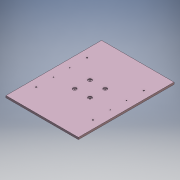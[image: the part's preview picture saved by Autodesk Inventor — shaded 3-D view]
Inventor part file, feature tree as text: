
AUTODESK INVENTOR PART (.ipt)
format: ipt  version: 2016 (Build 200138000, 138)  size: 162,304 bytes
history: native  units: mm
features: sketch x5, hole x3, extrude x2
ambient origin geometry x8: Origin, YZ Plane, XZ Plane, XY Plane, X Axis, Y Axis, Z Axis, Center Point
bodies: Solid1 (feature_tree)
feature tree (10):
  extrude  "baseExtrusion"  Depth=296.0mm
  hole  "xyStageAttach_m5"  [1 undecoded]
  hole  "zStageAttach_m6"  [1 undecoded]
  extrude  "attachmentExtrusion"  Depth=4.8mm
  hole  "postAttach_m6"  [1 undecoded]
  sketch  "Sketch1"  dims[d0=400.0mm d1=296.0mm]
  sketch  "Sketch2"  dims[d2=148.0mm d3=200.0mm]
  sketch  "Sketch4"  dims[d4=10.0mm d5=0.0mm d6=8.5mm]
  sketch  "Sketch5"  dims[d7=8.5mm]
  sketch  "Sketch9"  dims[d8=4.134mm d9=10.0mm d10=4.0mm d11=2.0mm d12=90.0deg d13=14.2mm d14=20.594885mm d22=160.0mm d23=240.0mm d24=75.0mm d25=75.0mm d26=37.5mm d27=37.5mm d28=6.6mm d29=12.0mm d30=18.0mm d31=4.8mm d32=90.0deg d33=17.1mm d34=20.594885mm d35=30.0mm d36=30.0mm d37=35.0mm d38=35.0mm d39=10.0mm d40=0.0mm d67=250.0mm d69=279.0mm d70=139.5mm d71=6.6mm d72=12.0mm d73=18.0mm d74=4.8mm d75=90.0deg d76=17.1mm d77=20.594885mm d78=125.0mm]
note: 3 required parameter values undecoded (feature->parameter linkage not recoverable at this tier; creation-order binding heuristic only, values carry confidence <= 0.55)
